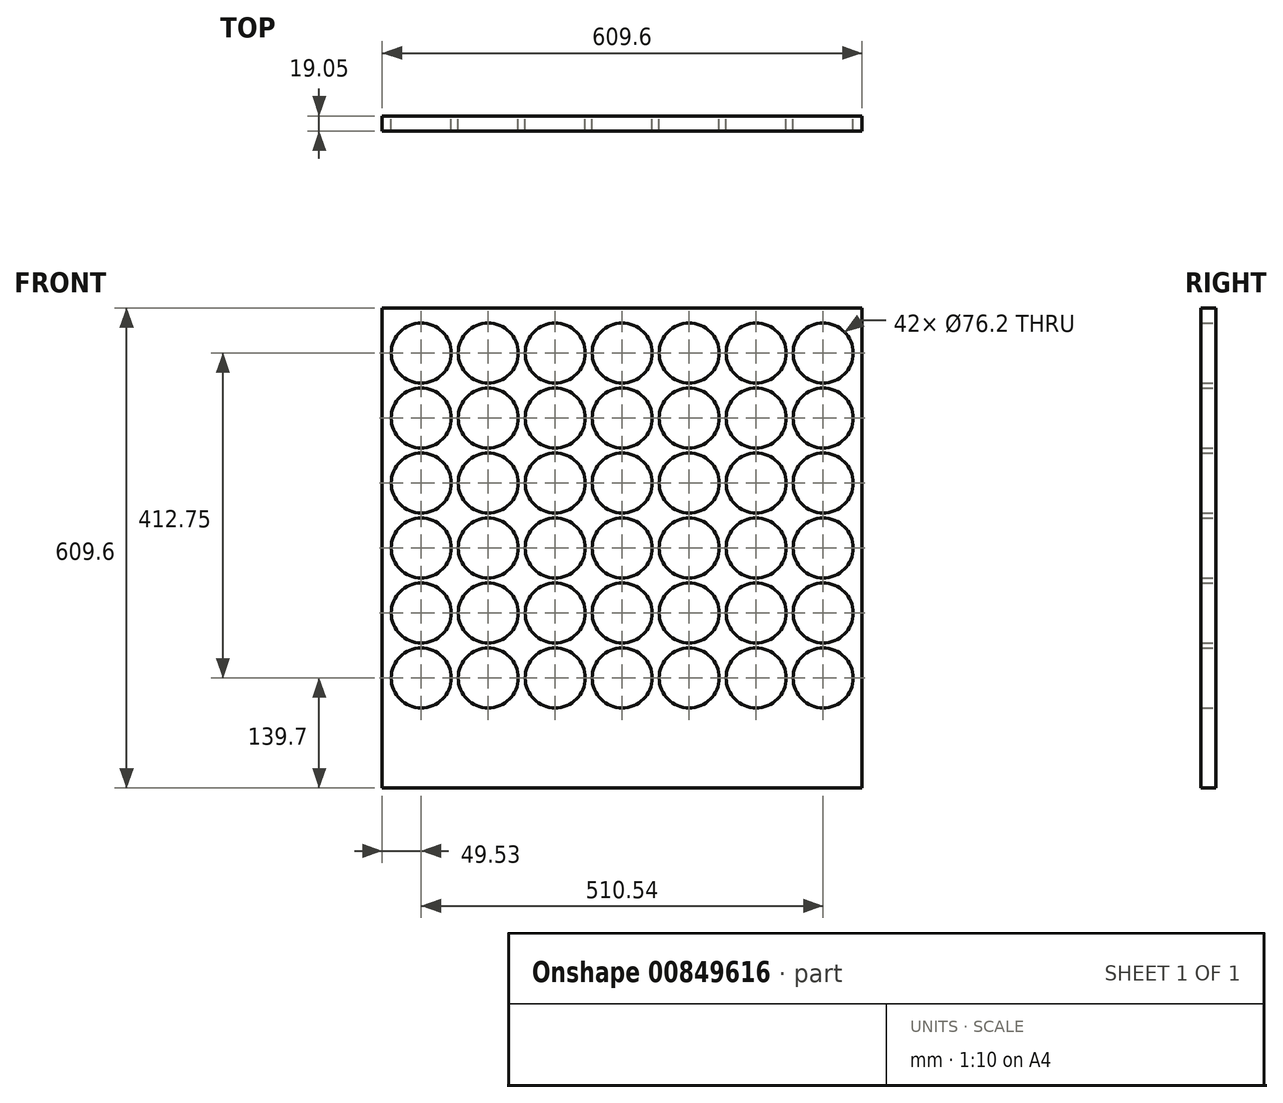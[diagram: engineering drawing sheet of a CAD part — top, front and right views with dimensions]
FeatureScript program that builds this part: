
annotation { "Feature Type Name" : "Feature", "Feature Type Description" : "" }
export const myFeature = defineFeature(function(context is Context, id is Id, definition is map)
    precondition{}
    {
        {
            var Q0;
            Q0=qCreatedBy(makeId("Front.planeOp"),FACE);
            var sketch = newSketch(context, id + "F0", { "sketchPlane" : qUnion([Q0])});
            skLineSegment(sketch, "E0.bottom", {"start": v(-304.8, 304.8) * mm, "end": v(304.8, 304.8) * mm});
            skLineSegment(sketch, "E0.top", {"start": v(-304.8, -304.8) * mm, "end": v(304.8, -304.8) * mm});
            skLineSegment(sketch, "E0.left", {"start": v(-304.8, 304.8) * mm, "end": v(-304.8, -304.8) * mm});
            skLineSegment(sketch, "E0.right", {"start": v(304.8, 304.8) * mm, "end": v(304.8, -304.8) * mm});
            skPoint(sketch, "E0.middle", {"position": v(0, 0) * mm});
            skCircle(sketch, "E1", {"center": v(-255.27, 247.65) * mm, "radius": 38.1 * mm});
            skCircle(sketch, "E2.0.1.0", {"center": v(-255.27, 165.1) * mm, "radius": 38.1 * mm});
            skCircle(sketch, "E2.0.2.0", {"center": v(-255.27, 82.55) * mm, "radius": 38.1 * mm});
            skCircle(sketch, "E2.0.3.0", {"center": v(-255.27, 0) * mm, "radius": 38.1 * mm});
            skCircle(sketch, "E2.0.4.0", {"center": v(-255.27, -82.55) * mm, "radius": 38.1 * mm});
            skCircle(sketch, "E2.0.5.0", {"center": v(-255.27, -165.1) * mm, "radius": 38.1 * mm});
            skCircle(sketch, "E2.1.0.0", {"center": v(-170.18, 247.65) * mm, "radius": 38.1 * mm});
            skCircle(sketch, "E2.1.1.0", {"center": v(-170.18, 165.1) * mm, "radius": 38.1 * mm});
            skCircle(sketch, "E2.1.2.0", {"center": v(-170.18, 82.55) * mm, "radius": 38.1 * mm});
            skCircle(sketch, "E2.1.3.0", {"center": v(-170.18, 0) * mm, "radius": 38.1 * mm});
            skCircle(sketch, "E2.1.4.0", {"center": v(-170.18, -82.55) * mm, "radius": 38.1 * mm});
            skCircle(sketch, "E2.1.5.0", {"center": v(-170.18, -165.1) * mm, "radius": 38.1 * mm});
            skCircle(sketch, "E2.2.0.0", {"center": v(-85.1, 247.65) * mm, "radius": 38.1 * mm});
            skCircle(sketch, "E2.2.1.0", {"center": v(-85.1, 165.1) * mm, "radius": 38.1 * mm});
            skCircle(sketch, "E2.2.2.0", {"center": v(-85.1, 82.55) * mm, "radius": 38.1 * mm});
            skCircle(sketch, "E2.2.3.0", {"center": v(-85.1, 0) * mm, "radius": 38.1 * mm});
            skCircle(sketch, "E2.2.4.0", {"center": v(-85.1, -82.55) * mm, "radius": 38.1 * mm});
            skCircle(sketch, "E2.2.5.0", {"center": v(-85.1, -165.1) * mm, "radius": 38.1 * mm});
            skCircle(sketch, "E2.3.0.0", {"center": v(0, 247.65) * mm, "radius": 38.1 * mm});
            skCircle(sketch, "E2.3.1.0", {"center": v(0, 165.1) * mm, "radius": 38.1 * mm});
            skCircle(sketch, "E2.3.2.0", {"center": v(0, 82.55) * mm, "radius": 38.1 * mm});
            skCircle(sketch, "E2.3.3.0", {"center": v(0, 0) * mm, "radius": 38.1 * mm});
            skCircle(sketch, "E2.3.4.0", {"center": v(0, -82.55) * mm, "radius": 38.1 * mm});
            skCircle(sketch, "E2.3.5.0", {"center": v(0, -165.1) * mm, "radius": 38.1 * mm});
            skCircle(sketch, "E2.4.0.0", {"center": v(85.1, 247.65) * mm, "radius": 38.1 * mm});
            skCircle(sketch, "E2.4.1.0", {"center": v(85.1, 165.1) * mm, "radius": 38.1 * mm});
            skCircle(sketch, "E2.4.2.0", {"center": v(85.1, 82.55) * mm, "radius": 38.1 * mm});
            skCircle(sketch, "E2.4.3.0", {"center": v(85.1, 0) * mm, "radius": 38.1 * mm});
            skCircle(sketch, "E2.4.4.0", {"center": v(85.1, -82.55) * mm, "radius": 38.1 * mm});
            skCircle(sketch, "E2.4.5.0", {"center": v(85.1, -165.1) * mm, "radius": 38.1 * mm});
            skCircle(sketch, "E2.5.0.0", {"center": v(170.18, 247.65) * mm, "radius": 38.1 * mm});
            skCircle(sketch, "E2.5.1.0", {"center": v(170.18, 165.1) * mm, "radius": 38.1 * mm});
            skCircle(sketch, "E2.5.2.0", {"center": v(170.18, 82.55) * mm, "radius": 38.1 * mm});
            skCircle(sketch, "E2.5.3.0", {"center": v(170.18, 0) * mm, "radius": 38.1 * mm});
            skCircle(sketch, "E2.5.4.0", {"center": v(170.18, -82.55) * mm, "radius": 38.1 * mm});
            skCircle(sketch, "E2.5.5.0", {"center": v(170.18, -165.1) * mm, "radius": 38.1 * mm});
            skCircle(sketch, "E2.6.0.0", {"center": v(255.27, 247.65) * mm, "radius": 38.1 * mm});
            skCircle(sketch, "E2.6.1.0", {"center": v(255.27, 165.1) * mm, "radius": 38.1 * mm});
            skCircle(sketch, "E2.6.2.0", {"center": v(255.27, 82.55) * mm, "radius": 38.1 * mm});
            skCircle(sketch, "E2.6.3.0", {"center": v(255.27, 0) * mm, "radius": 38.1 * mm});
            skCircle(sketch, "E2.6.4.0", {"center": v(255.27, -82.55) * mm, "radius": 38.1 * mm});
            skCircle(sketch, "E2.6.5.0", {"center": v(255.27, -165.1) * mm, "radius": 38.1 * mm});
            skLineSegment(sketch, "E2.direction1", {"start": v(-255.27, 247.65) * mm, "end": v(-170.18, 247.65) * mm, "construction": true});
            skLineSegment(sketch, "E2.direction2", {"start": v(-255.27, 247.65) * mm, "end": v(-255.27, 165.1) * mm, "construction": true});
            skSolve(sketch);
        }
        {
            var Q0;
            Q0 = qSketchRegion(id + "F0", true);
            extrude(context, id + "F1", {"entities" : qUnion([Q0]), "depth" : 19.05 * mm, "offsetDistance" : 25.4 * mm});
        }
    });
